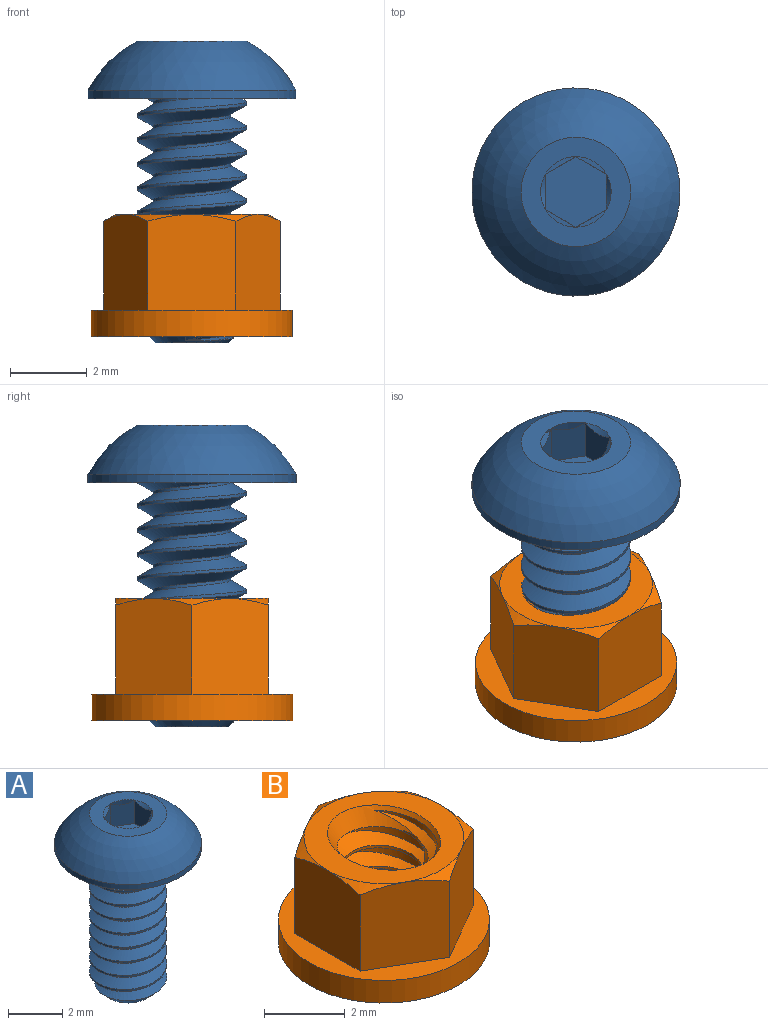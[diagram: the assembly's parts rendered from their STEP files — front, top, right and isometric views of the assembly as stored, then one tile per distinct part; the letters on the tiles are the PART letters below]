
ASSEMBLY  parts=2 mates=1
PART A: 24 faces, bbox 5.8x5.8x8.4 mm
  f0: cylinder r=1.42mm len=5.87mm, axis (0,0,-1), area 9.6mm2, adj f2,f4,f6,f9
  f1: cone r=0.95mm half-angle=45deg, axis (0,0,1), area 2.1mm2, adj f2,f3,f4,f5
  f2: cone r=0.95mm half-angle=45deg, axis (0,0,1), area 0.6mm2, adj f0,f1,f4,f6
  f3: plane 1.89x1.89mm, normal (0,0,-1), area 2.8mm2, adj f1
  f4: bspline ~6.91x3.29mm, area 35mm2, adj f0,f1,f2,f5,f9
  f5: cylinder r=1.01mm len=6.29mm, axis (0,0,-1), area 3.5mm2, adj f1,f4,f6,f9
  f6: bspline ~6.69x3.29mm, area 34.7mm2, adj f0,f2,f5,f9
  f7: sphere r=3.07mm, area 24.5mm2, adj f8,f10
  f8: plane 2.85x2.85mm, normal (0,0,1), area 3.7mm2, adj f7,f11,f12,f13,f14,f15,f16
  f9: plane 5.66x5.66mm, normal (0,0,-1), area 18.3mm2, adj f0,f4,f5,f6,f10
  f10: cylinder r=2.71mm len=5.41mm, axis (0,0,1), area 3.8mm2, adj f7,f9
  f11: cone r=0.92mm half-angle=45deg, axis (0,0,1), area 0mm2, adj f8,f18
  f12: cone r=0.92mm half-angle=45deg, axis (0,0,1), area 0mm2, adj f8,f19
  f13: cone r=0.92mm half-angle=45deg, axis (0,0,1), area 0mm2, adj f8,f20
  f14: cone r=0.92mm half-angle=45deg, axis (0,0,1), area 0mm2, adj f8,f21
  f15: cone r=0.92mm half-angle=45deg, axis (0,0,1), area 0mm2, adj f8,f22
  f16: cone r=0.92mm half-angle=45deg, axis (0,0,1), area 0mm2, adj f8,f23
  f17: plane 1.83x1.59mm, normal (0,0,1), area 2.2mm2, adj f18,f19,f20,f21,f22,f23
  f18: plane 1.4x1.27mm, normal (-1,0,0), area 0.9mm2, adj f11,f17,f19,f23
  f19: plane 1.4x1.14mm, normal (-0.5,-0.87,0), area 0.9mm2, adj f12,f17,f18,f20
  f20: plane 1.4x1.14mm, normal (0.5,-0.87,0), area 0.9mm2, adj f13,f17,f19,f21
  f21: plane 1.4x1.27mm, normal (1,0,0), area 0.9mm2, adj f14,f17,f20,f22
  f22: plane 1.4x1.14mm, normal (0.5,0.87,0), area 0.9mm2, adj f15,f17,f21,f23
  f23: plane 1.4x1.14mm, normal (-0.5,0.87,0), area 0.9mm2, adj f16,f17,f18,f22
PART B: 26 faces, bbox 5.4x5.4x3.8 mm
  f0: cylinder r=1.01mm len=2.13mm, axis (0,0,1), area 1.7mm2, adj f1,f2,f23,f24,f25
  f1: bspline ~1.33x1.09mm, area 0mm2, adj f0,f2
  f2: bspline ~3.29x3.1mm, area 12.6mm2, adj f0,f1,f3,f5,f6,f23,f25
  f3: extruded ~2.96x2.84mm, area 8.1mm2, adj f2,f4,f6,f23,f24
  f4: bspline ~3.29x2.85mm, area 0mm2, adj f3,f6
  f5: cylinder r=1.01mm len=1.2mm, axis (0,0,1), area 0.1mm2, adj f2,f6,f24,f25
  f6: bspline ~2.99x2.58mm, area 2.5mm2, adj f2,f3,f4,f5,f7,f24
  f7: plane 3.98x3.98mm, normal (0,0,1), area 6.3mm2, adj f6,f8,f18,f19,f20,f21,f22
  f8: cone r=1.98mm half-angle=60deg, axis (0,0,-1), area 0.4mm2, adj f7,f9,f17
  f9: plane 2.68x2.17mm, normal (-0.5,-0.87,0), area 5.6mm2, adj f8,f10,f16,f17,f18
  f10: plane 5.23x5.23mm, normal (0,0,1), area 7.9mm2, adj f9,f11,f12,f13,f14,f16,f17
  f11: plane 2.68x2.17mm, normal (0.5,0.87,0), area 5.6mm2, adj f10,f12,f13,f20,f21
  f12: plane 2.68x2.17mm, normal (-0.5,0.87,0), area 5.6mm2, adj f10,f11,f16,f19,f20
  f13: plane 2.68x2.48mm, normal (1,0,0), area 5.6mm2, adj f10,f11,f17,f21,f22
  f14: cylinder r=2.62mm len=5.23mm, axis (0,0,-1), area 11.3mm2, adj f10,f15
  f15: plane 5.24x5.24mm, normal (0,0,-1), area 15.4mm2, adj f14,f23
  f16: plane 2.68x2.48mm, normal (-1,0,0), area 5.6mm2, adj f9,f10,f12,f18,f19
  f17: plane 2.68x2.17mm, normal (0.5,-0.87,0), area 5.6mm2, adj f8,f9,f10,f13,f22
  f18: cone r=1.98mm half-angle=60deg, axis (0,0,-1), area 0.4mm2, adj f7,f9,f16
  f19: cone r=1.98mm half-angle=60deg, axis (0,0,-1), area 0.4mm2, adj f7,f12,f16
  f20: cone r=1.98mm half-angle=60deg, axis (0,0,-1), area 0.4mm2, adj f7,f11,f12
  f21: cone r=1.98mm half-angle=60deg, axis (0,0,-1), area 0.4mm2, adj f7,f11,f13
  f22: cone r=1.98mm half-angle=60deg, axis (0,0,-1), area 0.4mm2, adj f7,f13,f17
  f23: bspline ~3x2.58mm, area 2.7mm2, adj f0,f2,f3,f15,f24
  f24: bspline ~3.31x3.3mm, area 10.3mm2, adj f0,f3,f5,f6,f23,f25
  f25: bspline ~1.51x0.85mm, area 0.3mm2, adj f0,f2,f5,f24
PLACE A t=(4.93,7.41,6.25)mm
PLACE B rot(axis=(0,0,1),90deg) t=(4.93,7.41,0.15)mm
MATE slider A.f0 <-> B.f0  axis (0,0,-1) through (4.93,7.41,-1.6)mm
